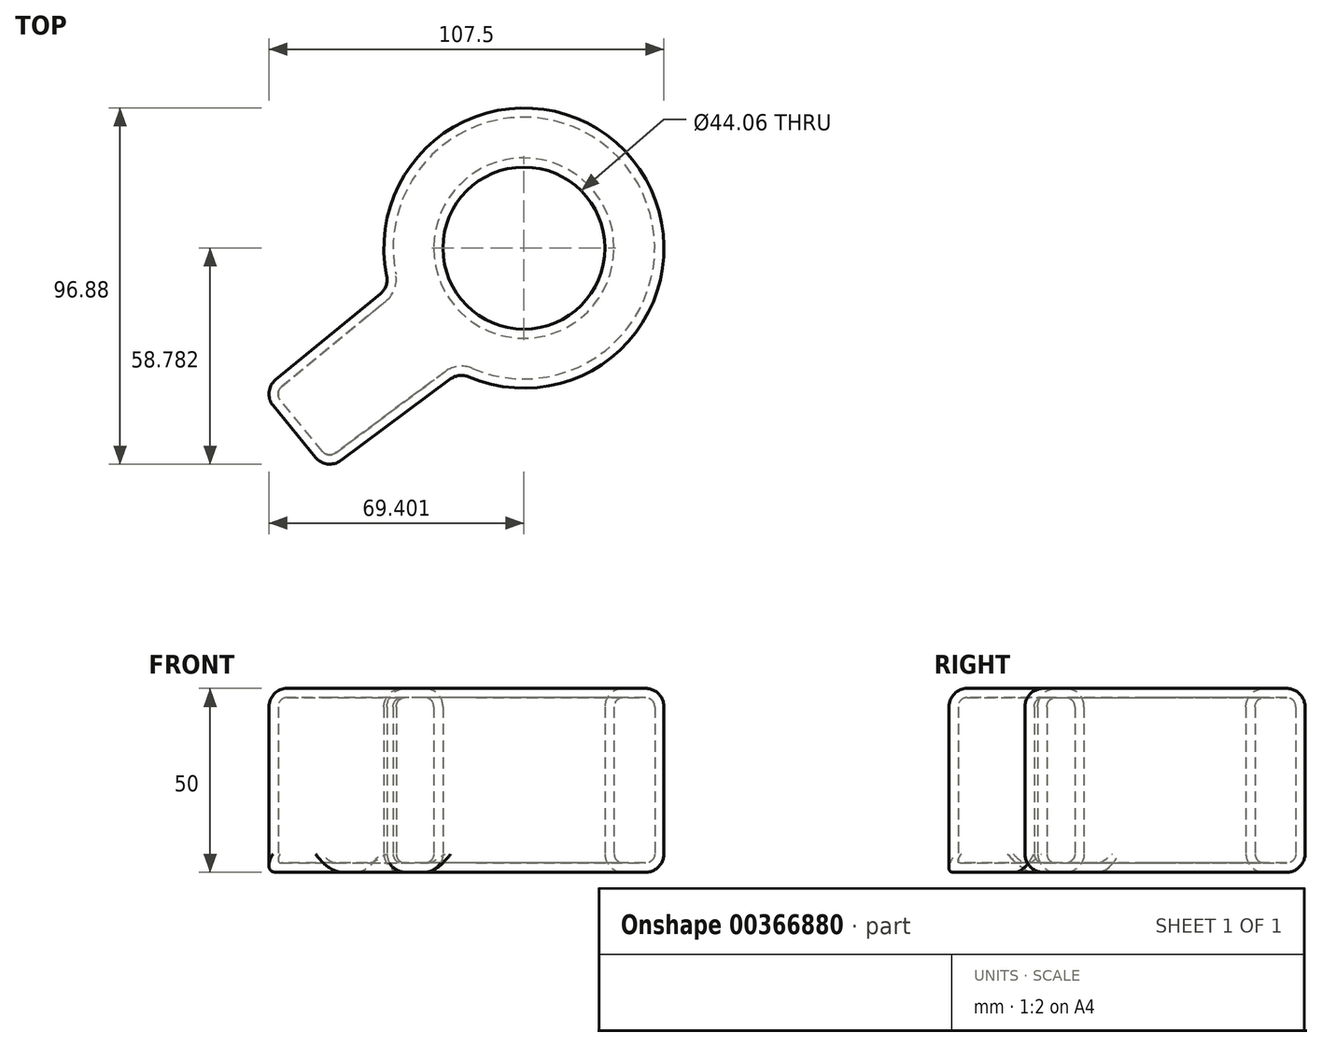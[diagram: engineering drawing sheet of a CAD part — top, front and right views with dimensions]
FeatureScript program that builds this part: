
annotation { "Feature Type Name" : "Feature", "Feature Type Description" : "" }
export const myFeature = defineFeature(function(context is Context, id is Id, definition is map)
    precondition{}
    {
        {
            var Q0;
            Q0=qCreatedBy(makeId("Top.planeOp"),FACE);
            var sketch = newSketch(context, id + "F0", { "sketchPlane" : qUnion([Q0])});
            skCircle(sketch, "E0", {"center": v(36.64, 26.93) * mm, "radius": 38.1 * mm});
            skCircle(sketch, "E1", {"center": v(36.64, 26.93) * mm, "radius": 22.03 * mm});
            skLineSegment(sketch, "E2", {"start": v(0, 16.49) * mm, "end": v(-34.8, -12.05) * mm});
            skLineSegment(sketch, "E3", {"start": v(-34.8, -12.05) * mm, "end": v(-17.04, -33.7) * mm});
            skLineSegment(sketch, "E4", {"start": v(-17.04, -33.7) * mm, "end": v(19.11, -6.9) * mm});
            skSolve(sketch);
        }
        {
            var Q0;
            Q0=qSketchRegion(id+"F0",true);
            extrude(context, id + "F1", {"entities" : qUnion([Q0]), "depth" : 50 * mm});
        }
        {
            var Q0;
            Q0=makeQuery(id+"F1.opExtrude","CAP_EDGE",EDGE,{"disambiguationData":[OSD([sQuery(id+"F0.wireOp",EDGE,"E0")])],"isStart":false});
            var Q1;
            Q1=makeQuery(id+"F1.opExtrude","CAP_EDGE",EDGE,{"disambiguationData":[OSD([sQuery(id+"F0.wireOp",EDGE,"E1")])],"isStart":false});
            var Q2;
            Q2=makeQuery(id+"F1.opExtrude","CAP_EDGE",EDGE,{"disambiguationData":[OSD([sQuery(id+"F0.wireOp",EDGE,"E2")])],"isStart":false});
            var Q3;
            Q3=makeQuery(id+"F1.opExtrude","CAP_EDGE",EDGE,{"disambiguationData":[OSD([sQuery(id+"F0.wireOp",EDGE,"E4")])],"isStart":false});
            var Q4;
            Q4=makeQuery(id+"F1.opExtrude","SWEPT_EDGE",EDGE,{"disambiguationData":[OSD([sQuery(id+"F0.wireOp",EDGE,"E0"),sQuery(id+"F0.wireOp",EDGE,"E2")])]});
            var Q5;
            Q5=makeQuery(id+"F1.opExtrude","SWEPT_EDGE",EDGE,{"disambiguationData":[OSD([sQuery(id+"F0.wireOp",EDGE,"E2"),sQuery(id+"F0.wireOp",EDGE,"E3")])]});
            var Q6;
            Q6=makeQuery(id+"F1.opExtrude","SWEPT_EDGE",EDGE,{"disambiguationData":[OSD([sQuery(id+"F0.wireOp",EDGE,"E0"),sQuery(id+"F0.wireOp",EDGE,"E4")])]});
            var Q7;
            Q7=makeQuery(id+"F1.opExtrude","SWEPT_EDGE",EDGE,{"disambiguationData":[OSD([sQuery(id+"F0.wireOp",EDGE,"E3"),sQuery(id+"F0.wireOp",EDGE,"E4")])]});
            var Q8;
            Q8=makeQuery(id+"F1.opExtrude","SWEPT_FACE",FACE,{"disambiguationData":[OSD([sQuery(id+"F0.wireOp",EDGE,"E3")])]});
            var Q9;
            Q9=makeQuery(id+"F1.opExtrude","CAP_EDGE",EDGE,{"disambiguationData":[OSD([sQuery(id+"F0.wireOp",EDGE,"E0")])],"isStart":true});
            var Q10;
            Q10=makeQuery(id+"F1.opExtrude","CAP_EDGE",EDGE,{"disambiguationData":[OSD([sQuery(id+"F0.wireOp",EDGE,"E1")])],"isStart":true});
            fillet(context, id + "F2", {"entities" : qUnion([Q0, Q1, Q2, Q3, Q4, Q5, Q6, Q7, Q8, Q9, Q10]), "radius" : 5 * mm, "tangentPropagation" : true, "allowEdgeOverflow" : false});
        }
        {
            var Q0;
            Q0=makeQuery(id+"F1.opExtrude","CAP_FACE",FACE,{"disambiguationData":[OSD([sQuery(id+"F0.wireOp",EDGE,"E0"),sQuery(id+"F0.wireOp",EDGE,"E1"),sQuery(id+"F0.wireOp",EDGE,"E2"),sQuery(id+"F0.wireOp",EDGE,"E3"),sQuery(id+"F0.wireOp",EDGE,"E4")])],"isStart":false});
            var Q1;
            Q1=makeQuery(id+"F1.opExtrude","SWEPT_BODY",BODY,{"disambiguationData":[OSD([sQuery(id+"F0.wireOp",EDGE,"E0"),sQuery(id+"F0.wireOp",EDGE,"E1"),sQuery(id+"F0.wireOp",EDGE,"E2"),sQuery(id+"F0.wireOp",EDGE,"E3"),sQuery(id+"F0.wireOp",EDGE,"E4")])]});
            shell(context, id + "F3", {"isHollow" : true, "entities" : qUnion([Q0]), "parts" : qUnion([Q1]), "thickness" : 2.5 * mm});
        }
    });
